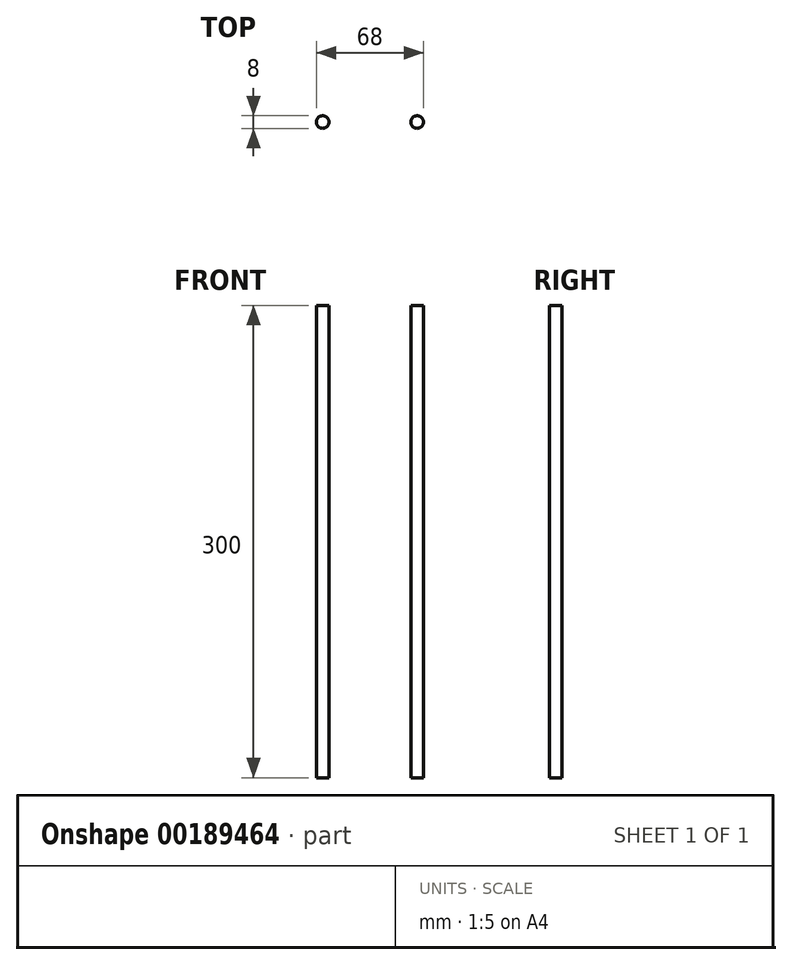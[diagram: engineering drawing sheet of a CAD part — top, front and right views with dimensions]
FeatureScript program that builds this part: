
annotation { "Feature Type Name" : "Feature", "Feature Type Description" : "" }
export const myFeature = defineFeature(function(context is Context, id is Id, definition is map)
    precondition{}
    {
        {
            var Q0;
            Q0=qCreatedBy(makeId("Top.planeOp"),FACE);
            var sketch = newSketch(context, id + "F0", { "sketchPlane" : qUnion([Q0])});
            skCircle(sketch, "E0", {"center": v(-52.35, 0) * mm, "radius": 4 * mm});
            skCircle(sketch, "E1", {"center": v(7.65, 0) * mm, "radius": 4 * mm});
            skSolve(sketch);
        }
        {
            var Q0;
            Q0=makeQuery(id+"F0.imprint","IMPRINT",FACE,{"disambiguationData":[TD([[makeQuery(id+"F0.imprint","IMPRINT",EDGE,{"derivedFrom":sQuery(id+"F0.wireOp",EDGE,"E1")}),1.0]])]});
            var Q1;
            Q1=makeQuery(id+"F0.imprint","IMPRINT",FACE,{"disambiguationData":[TD([[makeQuery(id+"F0.imprint","IMPRINT",EDGE,{"derivedFrom":sQuery(id+"F0.wireOp",EDGE,"E0")}),1.0]])]});
            extrude(context, id + "F1", {"entities" : qUnion([Q0, Q1]), "depth" : 300 * mm, "offsetDistance" : 25 * mm});
        }
    });
